# Revit family: 3031844 Lighting Fixture_Sylvania_Syl-Lighter II_Ceiling Recessed
name_source: partatom
category: Lighting Fixtures
revit_build: Autodesk Revit 2017 (Build: 20190507_1515(x64)
units: mm (PartAtom-declared; Revit-internal decimal feet)

## family parameters
Cut with Voids When Loaded = No
Host = Face
Light Source = Yes
OmniClass Number = 23.80.70.11.17
OmniClass Title = Specialized Lighting by Location or Use
Part Type = Normal
Room Calculation Point = No
Round Connector Dimension = Use Diameter
Shared = No

## types (1)
- Syl-Lighter LED II 195 RO 15W NW DALI
    Accessory Diameter = 195 mm  [stored 0.639764 ft]
    Accessory Material = Aluminum_Sylvania_Syl-Lighter LED II_White_RAL 9003
    Accessory Radius = 97.5 mm  [stored 0.319882 ft]
    Apparent Load = 16 VA
    Assembly Code = D5020200
    Beam Angle = 74.00°
    Body Material = Metal_Sylvania_Syl-Lighter LED II_Silver
    Catalog Number = 3031844 Syl-Lighter LED II 195 RO 16W NW DALI
    Color Filter = 16777215
    Cutout Diameter = 175 mm  [stored 0.574147 ft]
    Default Elevation = 0 mm  [stored 0 ft]
    Description = Ceiling recessed IP44 LED downlight, perfect where limited ceiling void is available with only 55mm product depth and 175mm cutout. Ideal replacement for 1x32W/2x18W CFL downlights. The polycarbonate diffuser allows for a wider light distribution and increased spacings between luminiares. Loop in loop out connector allows for quick installation. Die-cast aluminium body, 1575LM, 16W, 98lm/W, 4000K, Driver Current: 400mA, CRI80, 74° beam angle, Dli dimmable LED driver, IP44, IK07, 50,000 hrs (L70), (HxW) 55x195mm, 5 step MacAdam ellipse, 0.45kg, RAL9003, Class 2, 220-240V, energy class: A++, A+, A
    Diameter = 175 mm  [stored 0.574147 ft]
    Diffuser Diameter = 155 mm
    Diffuser Material = Polycarbonate_Sylvania_Syl-Lighter LED II_Opal
    Diffuser Radius = 77.5 mm
    Dimmable = DALI
    Dimming Lamp Color Temperature Shift = <None>
    Drive Current = 400mA
    Electrical Protection = CLASS II
    Emit Shape Visible in Rendering = No
    Emit from Circle Diameter = 155 mm
    Energy Class = A++, A+, A
    Glow Wire Test = 650 °C
    Height = 55 mm  [stored 0.180446 ft]
    IK Rating = IK07
    IP Rating = IP44
    Inner Diameter = 171 mm  [stored 0.561024 ft]
    Lamp = LED
    Lamp Comments = Integrated LED
    Life = 50 000h
    Manufacturer = Feilo Sylvania
    Model = SYL-LIGHTER LED II 195 RO 16W NW DALI
    Photometric Web File = 3031844.ies
    Product Family = SYL-LIGHTER LED II
    Product Page URL = http://www.sylvania-lighting.com
    Recessed Depth = 55 mm  [stored 0.180446 ft]
    Ta Rating = -10°C to +40°C
    Tilt Angle = -90.00°
    URL = http://www.sylvania-lighting.com
    Voltage = 240 V
    Voltage Comments = UNV (Universal Voltage; 220-240 Volt)
    Weight = 0.45 kg

note: [stored X ft] marks values corroborated as IEEE doubles in the binary element streams (Revit-internal decimal feet)

## geometry (parser evidence)
native form markers: Blend x4, Sweep x2
no freeform markers — native parametric forms only
